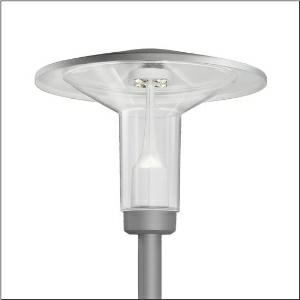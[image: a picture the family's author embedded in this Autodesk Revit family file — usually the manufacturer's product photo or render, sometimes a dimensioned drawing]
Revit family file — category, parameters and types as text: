
# Revit family: laterne_iq___st1_2a_5xa5255af14h_83bc
name_source: partatom
category: Lighting Fixtures
units: mm (PartAtom-declared; Revit-internal decimal feet)

## family parameters
Cut with Voids When Loaded = No
Host = Face
Light Source = No
Part Type = Normal
Room Calculation Point = No
Round Connector Dimension = Use Diameter
Shared = No

## types (1)
- --- (1 x LED, 1540 lm, 12.9 W, 2200K)
    Apparent Load = 13 VA
    CIE Flux Codes = 25 63 94 98 100
    Color Rendering = 70
    Color Temperature = 2200K
    Default Elevation = 1800 mm
    Description = Lantern iQ, mast luminaire, Module 540 iQ-SR, primary light control with 3 zone facetted reflector, of plastic, silver coated, highly specular, structured, primary optical cover: cover, of PMMA, transparent, light distribution: ST1.2a, light emission: direct distribution, primary light characteristic: asymmetric, installation type: post-top, LED, High Power LED, rated luminous flux: 1.540lm, luminous efficacy: 119lm/W, light colour: 722, colour temperature: 2200K, control gear: ECG iQ, control: presetting dimming logarithmic, Street-Remote, Auto-Match, Temp-Guard, Lumen-Switch, Night-Set, Smart-Wire, Light-Fading, Desk-Remote (wireless, voltage-free reading and setting of iQ features in the workshop via application-optimized NFC function/RFID function), optimised constant luminous flux control (CLO 2.0), with terminal, 6-pole, max. 2.5mm², mains connection: 220..240V, AC, 50/60Hz, start of lifetime: 13W, end of lifetime: 13W, reduction: 6W, luminaire housing, upper part, of glass-fibre reinforced polyester, coated, Siteco® metallic grey (DB 702S), diameter: 750mm, height: 583mm, spigot size: d x l = 76 x 70mm (post-top) | with reducer (optional accessory) 60 x 70mm, post-top mast mounting element, of diecast aluminium, coated, Siteco® metallic grey (DB 702S), Module 540 iQ-SR, traffic white (RAL 9016), equipment: standard, protection rating (complete): IP65, insulation class (complete): insulation class II (safety insulation), certification: CE, ENEC, VDE, packaging unit: 1 piece

Light Distribution: ST1.2a
    Height = 583 mm
    Lamp = 1 x LED
    Lamp Light Flux = 1540 lm
    Lamp Power = 12.9 W
    Lamp count = 1
    Length = 750 mm
    Luminous efficacy = 119 lm/W
    Manufacturer = Siteco
    ModVariant = No
    Model = 5XA5255AF14H
    Number of Poles = 1
    OnlyDefault = Yes
    Power Factor = 1
    Product Name = Laterne iQ | ST1.2a
    Product group = mast luminaire | pylon top
    ProductGroupID = 6100
    Protection Class = Protection class II
    Protection Degree = IP 65
    RLX_Detail_Level = 1
    RlxData = <blob elided: 103845 chars, md5=d73496e3>
    Socket = socket
    Standby Power = 0 W
    System Light Flux = 1540 lm
    System Power = 13 W
    Type Comments = factory setting: luminous flux: 100 % | dim-lin: 254 | 516 mA
    Type Image = l_1006050.jpg
    URL = http://relux.com
    VarID = @adj_071913
    Voltage = 0 V
    Weight = 0.00 kg
    Width = 0 mm  [stored 0 ft]

note: [stored X ft] marks values corroborated as IEEE doubles in the binary element streams (Revit-internal decimal feet)

## geometry (parser evidence)
native form markers: Blend x4, Sweep x11
no freeform markers — native parametric forms only
